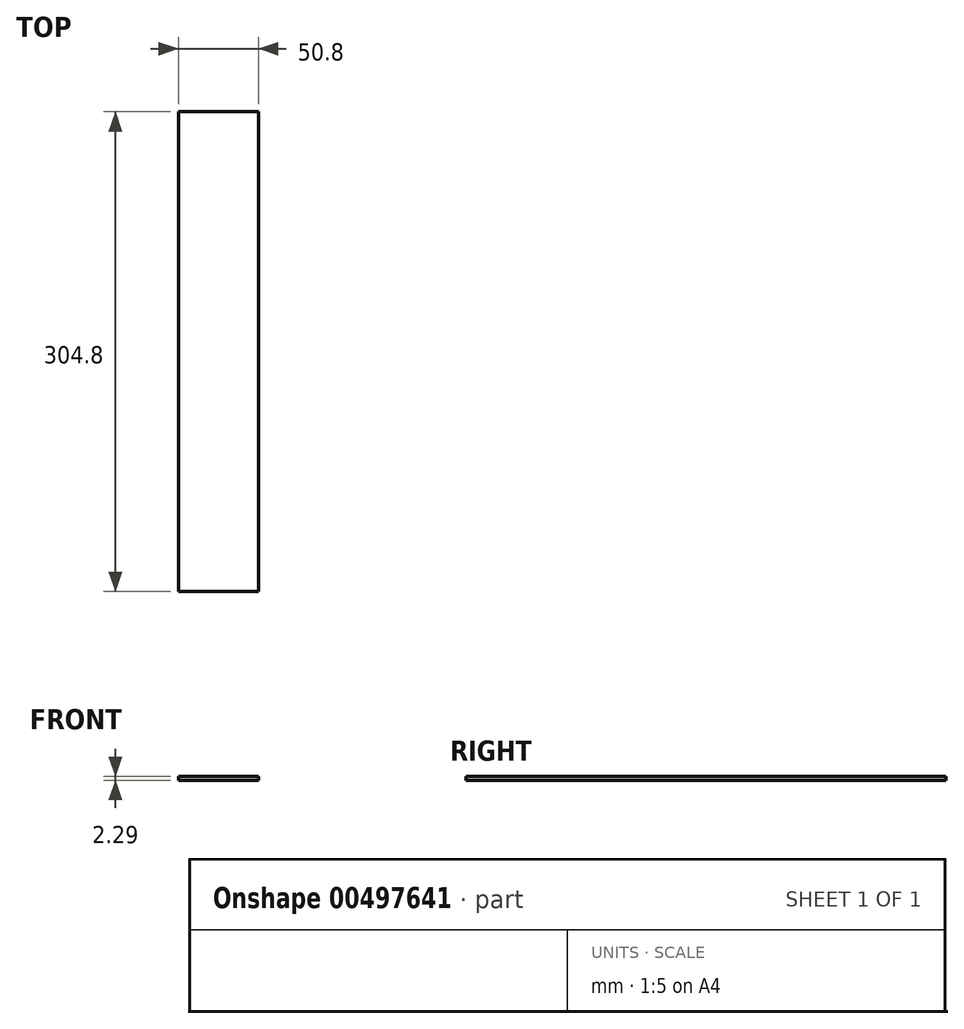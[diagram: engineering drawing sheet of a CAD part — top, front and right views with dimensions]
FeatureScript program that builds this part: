
annotation { "Feature Type Name" : "Feature", "Feature Type Description" : "" }
export const myFeature = defineFeature(function(context is Context, id is Id, definition is map)
    precondition{}
    {
        {
            var Q0;
            Q0=qCreatedBy(makeId("Top.planeOp"),FACE);
            var sketch = newSketch(context, id + "F0", { "sketchPlane" : qUnion([Q0])});
            skLineSegment(sketch, "E0.bottom", {"start": v(25.4, -152.4) * mm, "end": v(-25.4, -152.4) * mm});
            skLineSegment(sketch, "E0.top", {"start": v(25.4, 152.4) * mm, "end": v(-25.4, 152.4) * mm});
            skLineSegment(sketch, "E0.left", {"start": v(25.4, -152.4) * mm, "end": v(25.4, 152.4) * mm});
            skLineSegment(sketch, "E0.right", {"start": v(-25.4, -152.4) * mm, "end": v(-25.4, 152.4) * mm});
            skPoint(sketch, "E0.middle", {"position": v(0, 0) * mm});
            skSolve(sketch);
        }
        {
            var Q0;
            Q0 = qSketchRegion(id + "F0", true);
            extrude(context, id + "F1", {"entities" : qUnion([Q0]), "depth" : 2.3 * mm});
        }
    });
